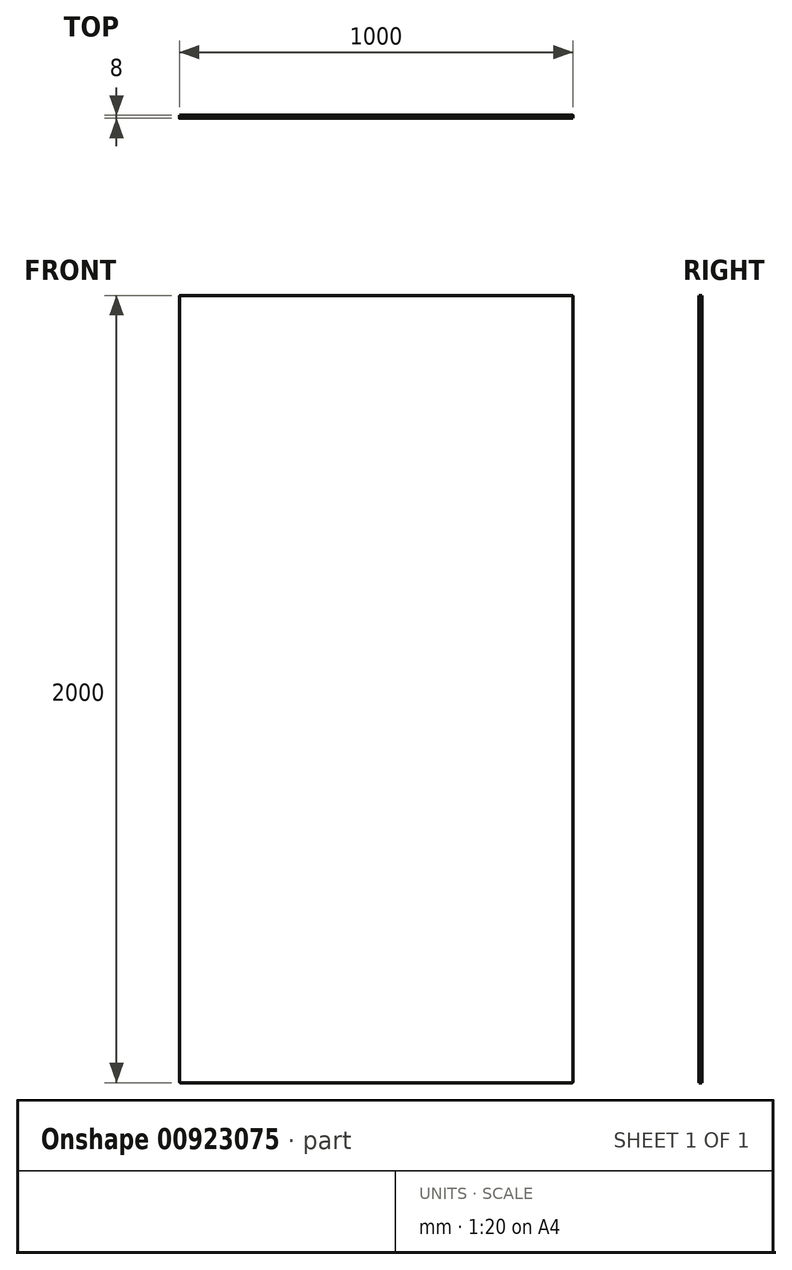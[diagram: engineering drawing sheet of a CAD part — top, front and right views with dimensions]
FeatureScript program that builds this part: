
annotation { "Feature Type Name" : "Feature", "Feature Type Description" : "" }
export const myFeature = defineFeature(function(context is Context, id is Id, definition is map)
    precondition{}
    {
        {
            var Q0;
            Q0=qCreatedBy(makeId("Front.planeOp"),FACE);
            var sketch = newSketch(context, id + "F0", { "sketchPlane" : qUnion([Q0])});
            skLineSegment(sketch, "E0.bottom", {"start": v(0, 0) * mm, "end": v(1000, 0) * mm});
            skLineSegment(sketch, "E0.top", {"start": v(0, 2000) * mm, "end": v(1000, 2000) * mm});
            skLineSegment(sketch, "E0.left", {"start": v(0, 0) * mm, "end": v(0, 2000) * mm});
            skLineSegment(sketch, "E0.right", {"start": v(1000, 0) * mm, "end": v(1000, 2000) * mm});
            skSolve(sketch);
        }
        {
            var Q0;
            Q0 = qSketchRegion(id + "F0", true);
            extrude(context, id + "F1", {"entities" : qUnion([Q0]), "depth" : 8 * mm, "offsetDistance" : 25 * mm});
        }
        {
            var Q0;
            Q0=makeQuery(id+"F1.opExtrude","SWEPT_EDGE",EDGE,{"disambiguationData":[OSD([sQuery(id+"F0.wireOp",EDGE,"E0.top"),sQuery(id+"F0.wireOp",EDGE,"E0.right")])]});
            var Q1;
            Q1=makeQuery(id+"F1.opExtrude","SWEPT_EDGE",EDGE,{"disambiguationData":[OSD([sQuery(id+"F0.wireOp",EDGE,"E0.top"),sQuery(id+"F0.wireOp",EDGE,"E0.left")])]});
            var Q2;
            Q2=makeQuery(id+"F1.opExtrude","SWEPT_EDGE",EDGE,{"disambiguationData":[OSD([sQuery(id+"F0.wireOp",EDGE,"E0.bottom"),sQuery(id+"F0.wireOp",EDGE,"E0.right")])]});
            var Q3;
            Q3=makeQuery(id+"F1.opExtrude","SWEPT_EDGE",EDGE,{"disambiguationData":[OSD([sQuery(id+"F0.wireOp",EDGE,"E0.bottom"),sQuery(id+"F0.wireOp",EDGE,"E0.left")])]});
            fillet(context, id + "F2", {"entities" : qUnion([Q0, Q1, Q2, Q3]), "radius" : 2 * mm, "tangentPropagation" : true, "allowEdgeOverflow" : false});
        }
    });
